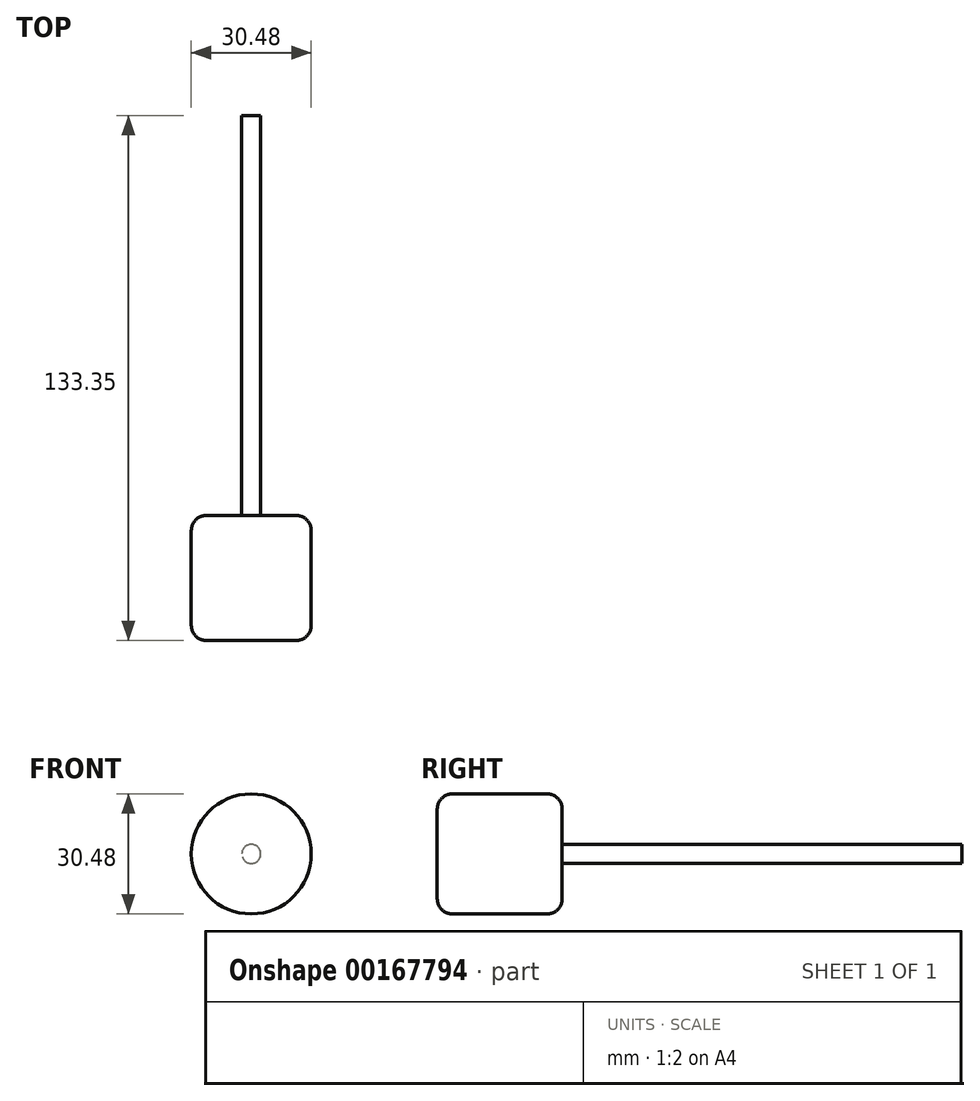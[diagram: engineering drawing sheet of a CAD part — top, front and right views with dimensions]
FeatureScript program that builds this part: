
annotation { "Feature Type Name" : "Feature", "Feature Type Description" : "" }
export const myFeature = defineFeature(function(context is Context, id is Id, definition is map)
    precondition{}
    {
        {
            var Q0;
            Q0=qCreatedBy(makeId("Front.planeOp"),FACE);
            var sketch = newSketch(context, id + "F0", { "sketchPlane" : qUnion([Q0])});
            skCircle(sketch, "E0", {"center": v(0, 0) * mm, "radius": 15.24 * mm});
            skSolve(sketch);
        }
        {
            var Q0;
            Q0=qSketchRegion(id+"F0",true);
            extrude(context, id + "F1", {"entities" : qUnion([Q0]), "depth" : 31.75 * mm});
        }
        {
            var Q0;
            Q0=makeQuery(id+"F1.opExtrude","CAP_EDGE",EDGE,{"disambiguationData":[OSD([sQuery(id+"F0.wireOp",EDGE,"E0")])],"isStart":false});
            var Q1;
            Q1=makeQuery(id+"F1.opExtrude","CAP_EDGE",EDGE,{"disambiguationData":[OSD([sQuery(id+"F0.wireOp",EDGE,"E0")])],"isStart":true});
            fillet(context, id + "F2", {"entities" : qUnion([Q0, Q1]), "radius" : 3.8 * mm, "tangentPropagation" : true, "allowEdgeOverflow" : false});
        }
        {
            var Q0;
            Q0=makeQuery(id+"F1.opExtrude","CAP_FACE",FACE,{"disambiguationData":[OSD([sQuery(id+"F0.wireOp",EDGE,"E0")])],"isStart":true});
            var sketch = newSketch(context, id + "F3", { "sketchPlane" : qUnion([Q0])});
            skCircle(sketch, "E1", {"center": v(0, 0) * mm, "radius": 2.41 * mm});
            skSolve(sketch);
        }
        {
            var Q0;
            Q0=qSketchRegion(id+"F3",true);
            extrude(context, id + "F4", {"entities" : qUnion([Q0]), "operationType" : NewBodyOperationType.ADD, "depth" : 101.6 * mm});
        }
    });
